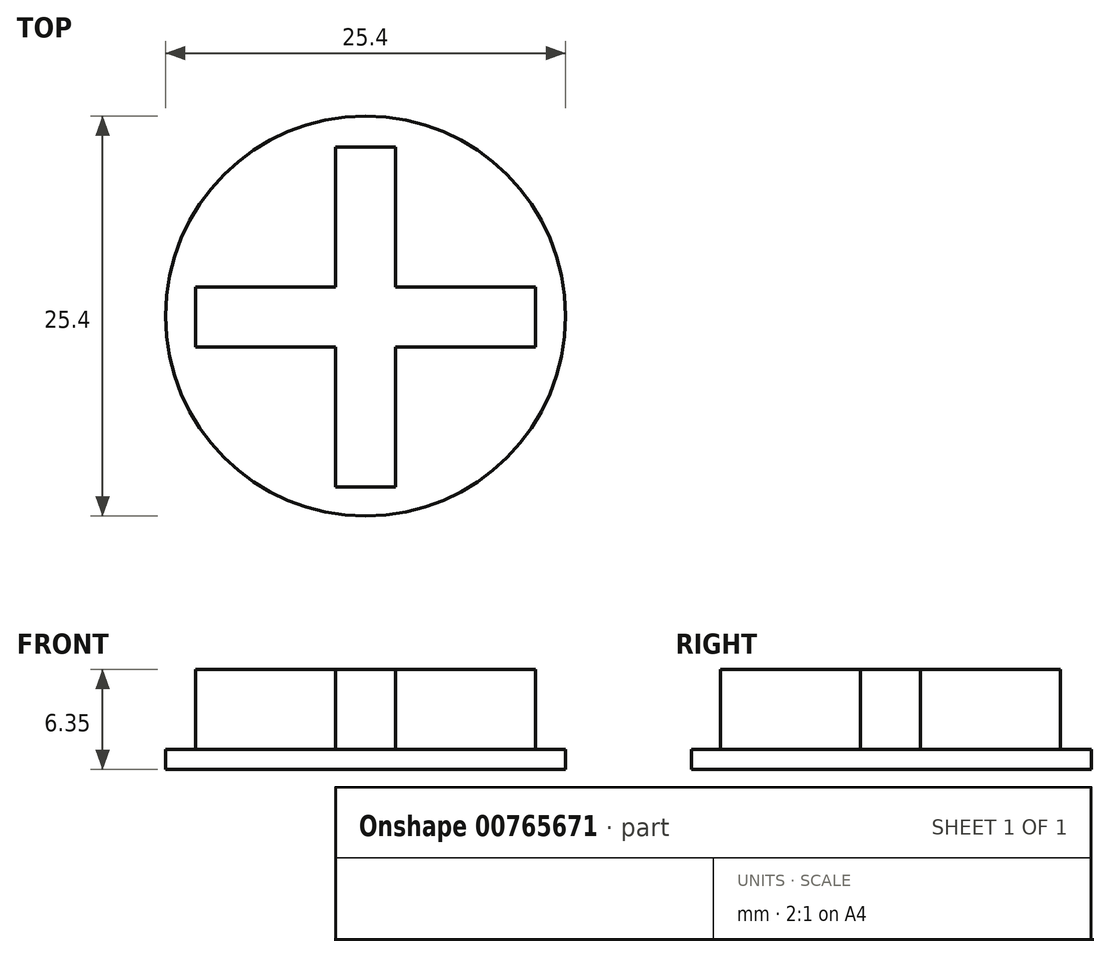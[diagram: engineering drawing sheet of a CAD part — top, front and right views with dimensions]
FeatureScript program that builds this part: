
annotation { "Feature Type Name" : "Feature", "Feature Type Description" : "" }
export const myFeature = defineFeature(function(context is Context, id is Id, definition is map)
    precondition{}
    {
        {
            var Q0;
            Q0=qCreatedBy(makeId("Top.planeOp"),FACE);
            var sketch = newSketch(context, id + "F0", { "sketchPlane" : qUnion([Q0])});
            skCircle(sketch, "E0", {"center": v(0, 0) * mm, "radius": 12.7 * mm});
            skSolve(sketch);
        }
        {
            var Q0;
            Q0 = qSketchRegion(id + "F0", true);
            extrude(context, id + "F1", {"entities" : qUnion([Q0]), "depth" : 1.27 * mm, "offsetDistance" : 25.4 * mm});
        }
        {
            var Q0;
            Q0=qCreatedBy(makeId("Top.planeOp"),FACE);
            cPlane(context, id + "F2", {"entities" : qUnion([Q0]), "cplaneType" : CPlaneType.OFFSET, "offset" : 1.27 * mm, "width" : 152.4 * mm, "height" : 152.4 * mm});
        }
        {
            var Q0;
            Q0=qCreatedBy(id+"F2.planeOp",FACE);
            var sketch = newSketch(context, id + "F3", { "sketchPlane" : qUnion([Q0])});
            skLineSegment(sketch, "E1", {"start": v(-1.9, 10.72) * mm, "end": v(1.9, 10.72) * mm});
            skLineSegment(sketch, "E2", {"start": v(1.9, 10.72) * mm, "end": v(1.9, 1.83) * mm});
            skLineSegment(sketch, "E3", {"start": v(1.9, 1.83) * mm, "end": v(10.8, 1.83) * mm});
            skLineSegment(sketch, "E4", {"start": v(10.8, 1.83) * mm, "end": v(10.8, -1.98) * mm});
            skLineSegment(sketch, "E5", {"start": v(10.8, -1.98) * mm, "end": v(1.9, -1.98) * mm});
            skLineSegment(sketch, "E6", {"start": v(1.9, -1.98) * mm, "end": v(1.9, -10.87) * mm});
            skLineSegment(sketch, "E7", {"start": v(1.9, -10.87) * mm, "end": v(-1.9, -10.87) * mm});
            skLineSegment(sketch, "E8", {"start": v(-1.9, -10.87) * mm, "end": v(-1.9, -1.98) * mm});
            skLineSegment(sketch, "E9", {"start": v(-1.9, -1.98) * mm, "end": v(-10.8, -1.98) * mm});
            skLineSegment(sketch, "E10", {"start": v(-10.8, -1.98) * mm, "end": v(-10.8, 1.83) * mm});
            skLineSegment(sketch, "E11", {"start": v(-10.8, 1.83) * mm, "end": v(-1.9, 1.83) * mm});
            skLineSegment(sketch, "E12", {"start": v(-1.9, 1.83) * mm, "end": v(-1.9, 10.72) * mm});
            skSolve(sketch);
        }
        {
            var Q0;
            Q0=makeQuery(id+"F3.imprint","IMPRINT",FACE,{"disambiguationData":[TD([[makeQuery(id+"F3.imprint","IMPRINT",EDGE,{"derivedFrom":sQuery(id+"F3.wireOp",EDGE,"E1")}),-1.0]])]});
            extrude(context, id + "F4", {"entities" : qUnion([Q0]), "operationType" : NewBodyOperationType.ADD, "depth" : 5.08 * mm, "offsetDistance" : 25.4 * mm});
        }
    });
